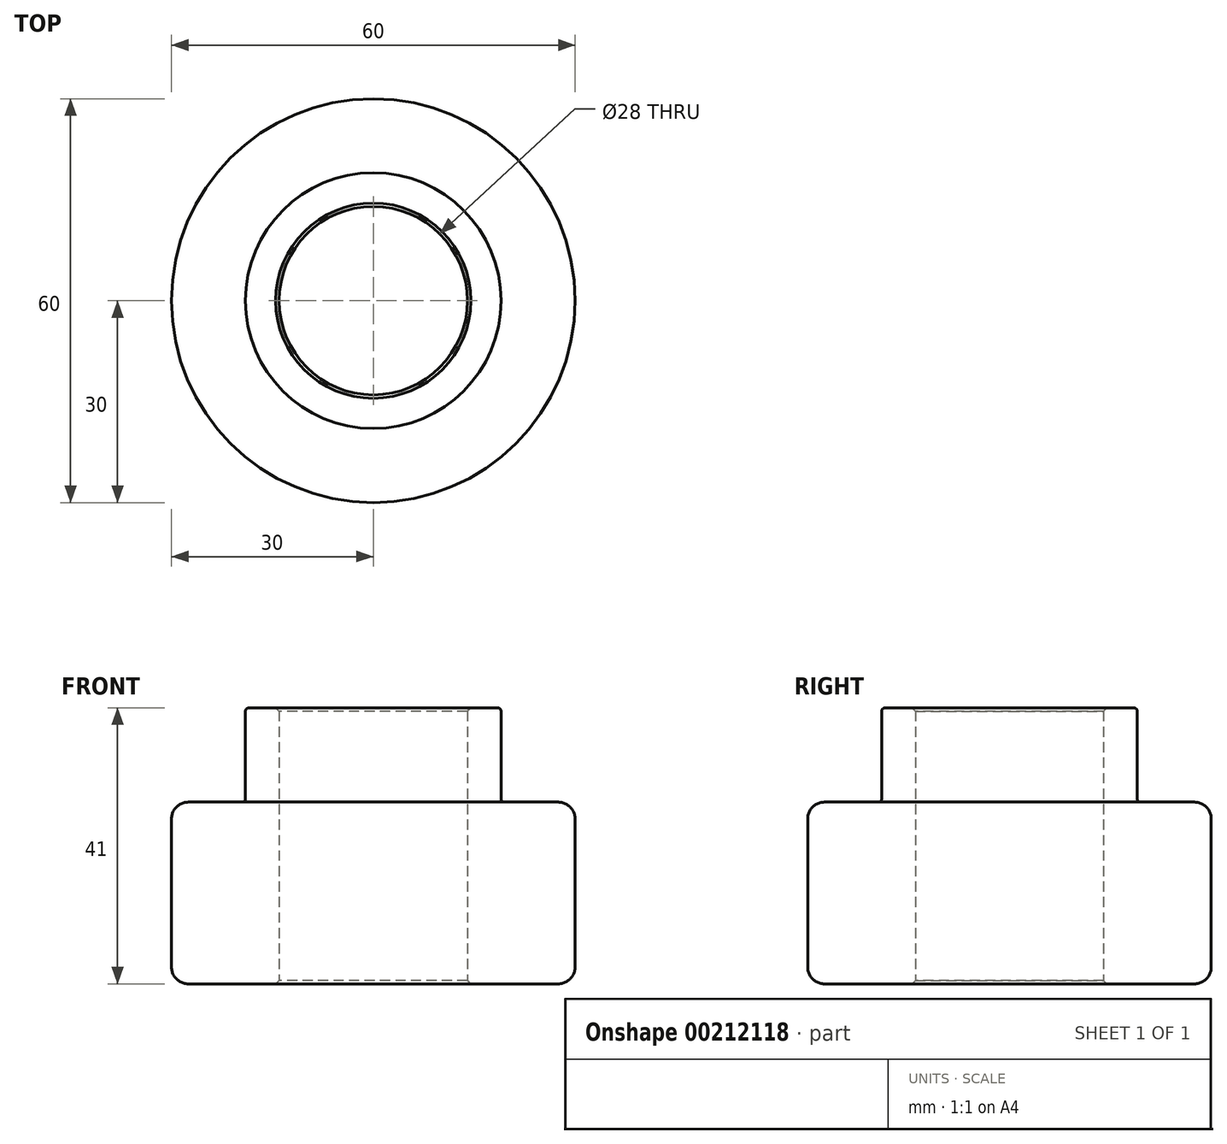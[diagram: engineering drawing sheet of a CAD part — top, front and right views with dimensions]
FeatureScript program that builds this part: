
annotation { "Feature Type Name" : "Feature", "Feature Type Description" : "" }
export const myFeature = defineFeature(function(context is Context, id is Id, definition is map)
    precondition{}
    {
        {
            var Q0;
            Q0=qCreatedBy(makeId("Top.planeOp"),FACE);
            var sketch = newSketch(context, id + "F0", { "sketchPlane" : qUnion([Q0])});
            skCircle(sketch, "E0", {"center": v(0, 0) * mm, "radius": 14 * mm});
            skCircle(sketch, "E1", {"center": v(0, 0) * mm, "radius": 19 * mm});
            skCircle(sketch, "E2", {"center": v(0, 0) * mm, "radius": 30 * mm});
            skSolve(sketch);
        }
        {
            var Q0;
            Q0=makeQuery(id+"F0.imprint","IMPRINT",FACE,{"disambiguationData":[TD([[makeQuery(id+"F0.imprint","IMPRINT",EDGE,{"derivedFrom":sQuery(id+"F0.wireOp",EDGE,"E1")}),-1.0]])]});
            var Q1;
            Q1=makeQuery(id+"F0.imprint","IMPRINT",FACE,{"disambiguationData":[TD([[makeQuery(id+"F0.imprint","IMPRINT",EDGE,{"derivedFrom":sQuery(id+"F0.wireOp",EDGE,"E0")}),-1.0]])]});
            extrude(context, id + "F1", {"entities" : qUnion([Q0, Q1]), "depth" : 27 * mm});
        }
        {
            var Q0;
            Q0=makeQuery(id+"F0.imprint","IMPRINT",FACE,{"disambiguationData":[TD([[makeQuery(id+"F0.imprint","IMPRINT",EDGE,{"derivedFrom":sQuery(id+"F0.wireOp",EDGE,"E0")}),-1.0]])]});
            extrude(context, id + "F2", {"entities" : qUnion([Q0]), "operationType" : NewBodyOperationType.ADD, "depth" : (27 + 14) * mm});
        }
        {
            var Q0;
            Q0=makeQuery(id+"F1.opExtrude","CAP_EDGE",EDGE,{"disambiguationData":[OSD([sQuery(id+"F0.wireOp",EDGE,"E2")])],"isStart":true});
            var Q1;
            Q1=makeQuery(id+"F1.opExtrude","CAP_EDGE",EDGE,{"disambiguationData":[OSD([sQuery(id+"F0.wireOp",EDGE,"E2")])],"isStart":false});
            fillet(context, id + "F3", {"entities" : qUnion([Q0, Q1]), "radius" : 2.5 * mm, "tangentPropagation" : true, "allowEdgeOverflow" : false});
        }
        {
            var Q0;
            Q0=makeQuery(id+"F2.boolean.opBoolean","INTERSECT",EDGE,{"derivedFrom":[makeQuery(id+"F1.opExtrude","CAP_FACE",FACE,{"disambiguationData":[OSD([sQuery(id+"F0.wireOp",EDGE,"E0"),sQuery(id+"F0.wireOp",EDGE,"E2")])],"isStart":false}),makeQuery(id+"F2.opExtrude","SWEPT_FACE",FACE,{"disambiguationData":[OSD([sQuery(id+"F0.wireOp",EDGE,"E1")])]})]});
            var Q1;
            Q1=makeQuery(id+"F2.opExtrude","CAP_EDGE",EDGE,{"disambiguationData":[OSD([sQuery(id+"F0.wireOp",EDGE,"E1")])],"isStart":false});
            fillet(context, id + "F4", {"entities" : qUnion([Q0, Q1]), "radius" : .5 * mm, "tangentPropagation" : true, "allowEdgeOverflow" : false});
        }
        {
            var Q0;
            Q0=makeQuery(id+"F2.opExtrude","CAP_EDGE",EDGE,{"disambiguationData":[OSD([sQuery(id+"F0.wireOp",EDGE,"E0")])],"isStart":false});
            var Q1;
            Q1=makeQuery(id+"F1.opExtrude","CAP_EDGE",EDGE,{"disambiguationData":[OSD([sQuery(id+"F0.wireOp",EDGE,"E0")])],"isStart":true});
            chamfer(context, id + "F5", {"entities" : qUnion([Q0, Q1]), "width" : .5 * mm, "tangentPropagation" : true});
        }
    });
